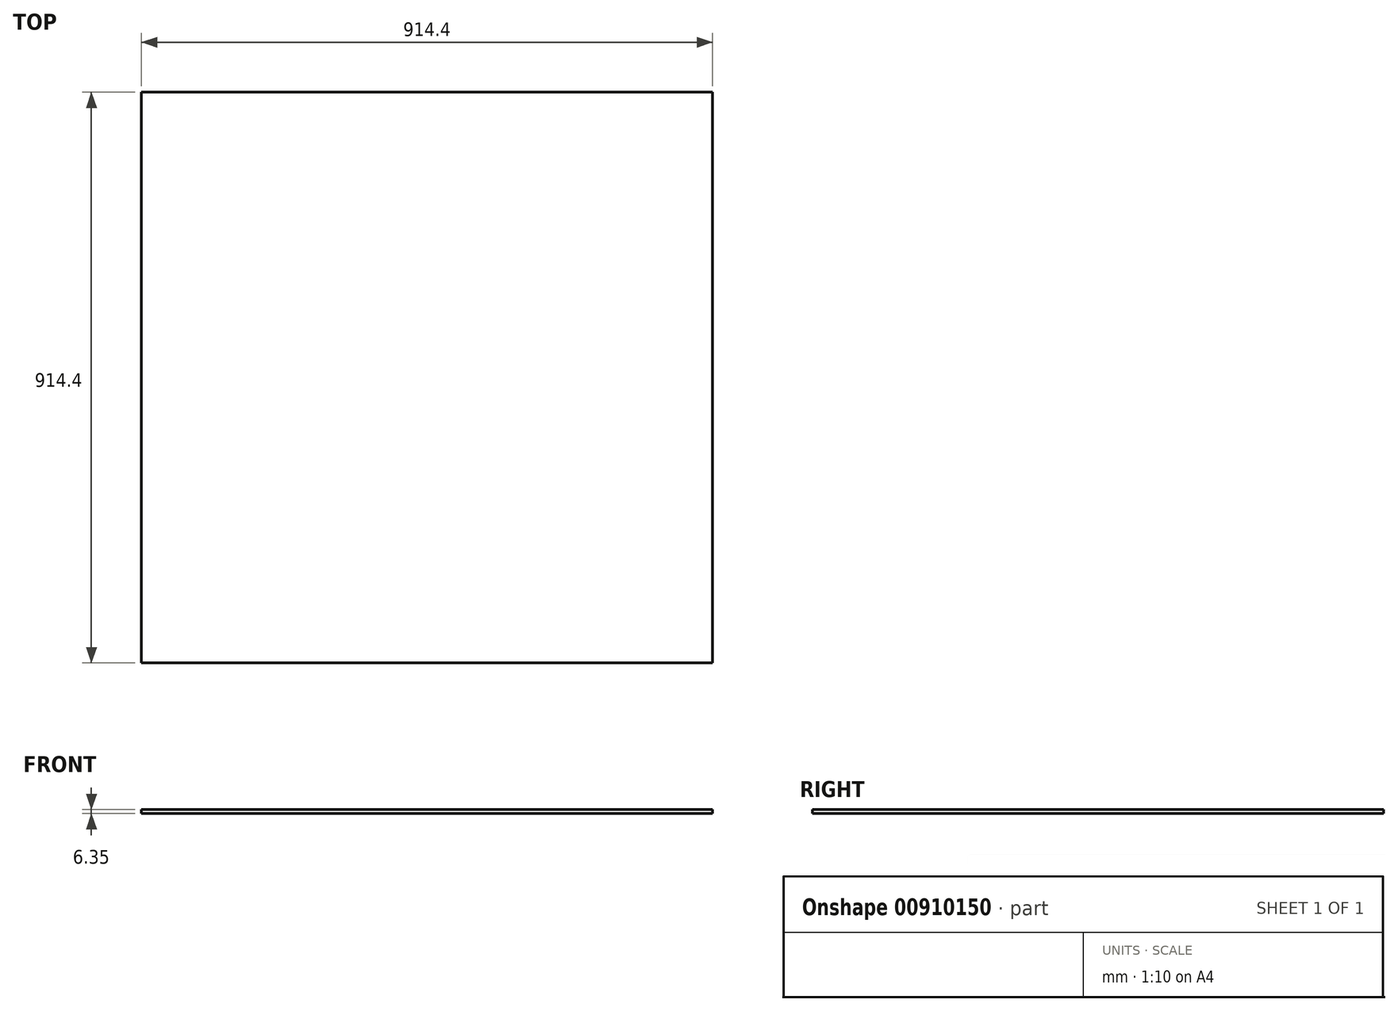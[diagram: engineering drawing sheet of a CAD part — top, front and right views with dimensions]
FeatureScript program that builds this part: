
annotation { "Feature Type Name" : "Feature", "Feature Type Description" : "" }
export const myFeature = defineFeature(function(context is Context, id is Id, definition is map)
    precondition{}
    {
        {
            var Q0;
            Q0=qCreatedBy(makeId("Top.planeOp"),FACE);
            var sketch = newSketch(context, id + "F0", { "sketchPlane" : qUnion([Q0])});
            skLineSegment(sketch, "E0.bottom", {"start": v(-1389.77, -475.33) * mm, "end": v(-475.37, -475.33) * mm});
            skLineSegment(sketch, "E0.top", {"start": v(-1389.77, 439.07) * mm, "end": v(-475.37, 439.07) * mm});
            skLineSegment(sketch, "E0.left", {"start": v(-1389.77, -475.33) * mm, "end": v(-1389.77, 439.07) * mm});
            skLineSegment(sketch, "E0.right", {"start": v(-475.37, -475.33) * mm, "end": v(-475.37, 439.07) * mm});
            skPoint(sketch, "E1", {"position": v(-475.37, -475.33) * mm});
            skSolve(sketch);
        }
        {
            var Q0;
            Q0 = qSketchRegion(id + "F0", true);
            extrude(context, id + "F1", {"entities" : qUnion([Q0]), "depth" : 6.35 * mm, "offsetDistance" : 25.4 * mm});
        }
    });
